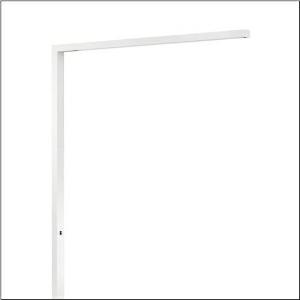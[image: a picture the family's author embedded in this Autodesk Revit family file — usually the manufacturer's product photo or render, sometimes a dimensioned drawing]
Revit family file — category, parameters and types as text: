
# Revit family: silica_r__11_floor_5mx51bs3wzk00002xx_06fb
name_source: partatom
category: Lighting Fixtures
units: mm (PartAtom-declared; Revit-internal decimal feet)

## family parameters
Cut with Voids When Loaded = No
Host = Face
Light Source = No
Part Type = Normal
Room Calculation Point = No
Round Connector Dimension = Use Diameter
Shared = No

## types (1)
- --- (1 x LED, 3960 lm / 8500 lm, 24.4 W / 54.9 W, 4000K)
    Apparent Load = 79 VA
    CIE Flux Codes = 82 97 100 100 100 / - - - 0 100
    Color Rendering = 80
    Color Temperature = 4000K
    Default Elevation = 1800 mm
    Description = Silica® 11 Floor, floorstanding luminaire, of PMMA, primary optical cover: cover panel, of PMMA, light emission: indirect/direct distribution, primary light characteristic: symmetric, installation type: not mounted, LED rated luminous flux: 12.460 lm, light colour: 840, colour temperature: 4000K, control gear: ECG DALI, daylight-dependent control, mains connection: 230V, AC, 50Hz, connection cable pre-assembled, cable length: 3 m, rated input power: 79W, luminaire head, rectangular, rounded, of aluminium, coated, traffic white (RAL 9016), supporting column, angular, of aluminium, coated, traffic white (RAL 9016), baseplate, of steel, coated, traffic white (RAL 9016), length: 1.316 mm, width: 65 mm, protection rating (complete): IP20, insulation class (complete): insulation class I (protective earthing), certification: CE, permissible ambient temperature for indoor applications: 0..+35°C, standard: EN 50419, packaging unit: 1 piece
    Height = 40 mm  [stored 0.131234 ft]
    Lamp = 1 x LED
    Lamp Light Flux = 3960 lm / 8500 lm
    Lamp Power = 24.4 W / 54.9 W
    Lamp count = 1
    Length = 1317 mm
    Luminous efficacy = 157 lm/W
    Manufacturer = Siteco
    ModVariant = No
    Model = 5MX51BS3WZK00002XX
    Mounting Place = Floor
    Mounting Type = Freestanding
    Number of Poles = 1
    OnlyDefault = Yes
    Power Factor = 1
    Product Name = Silica® 11 Floor
    Product group = floorstanding luminaire
    ProductGroupID = 1302
    Protection Class = Protection class I
    Protection Degree = IP 20
    RLX_Detail_Level = 1
    RlxData = <blob elided: 18141 chars, md5=b3f894b6>
    Socket = socket
    Standby Power = 0 W
    System Light Flux = 12460 lm
    System Power = 79 W
    Type Comments = factory setting: direct and indirect light
    Type Image = l_1004655.jpg
    URL = http://relux.com
    VarID = @adj_131716
    Voltage = 0 V
    Weight = 0.00 kg
    Width = 65 mm

note: [stored X ft] marks values corroborated as IEEE doubles in the binary element streams (Revit-internal decimal feet)

## geometry (parser evidence)
native form markers: Blend x4, Sweep x15
no freeform markers — native parametric forms only
